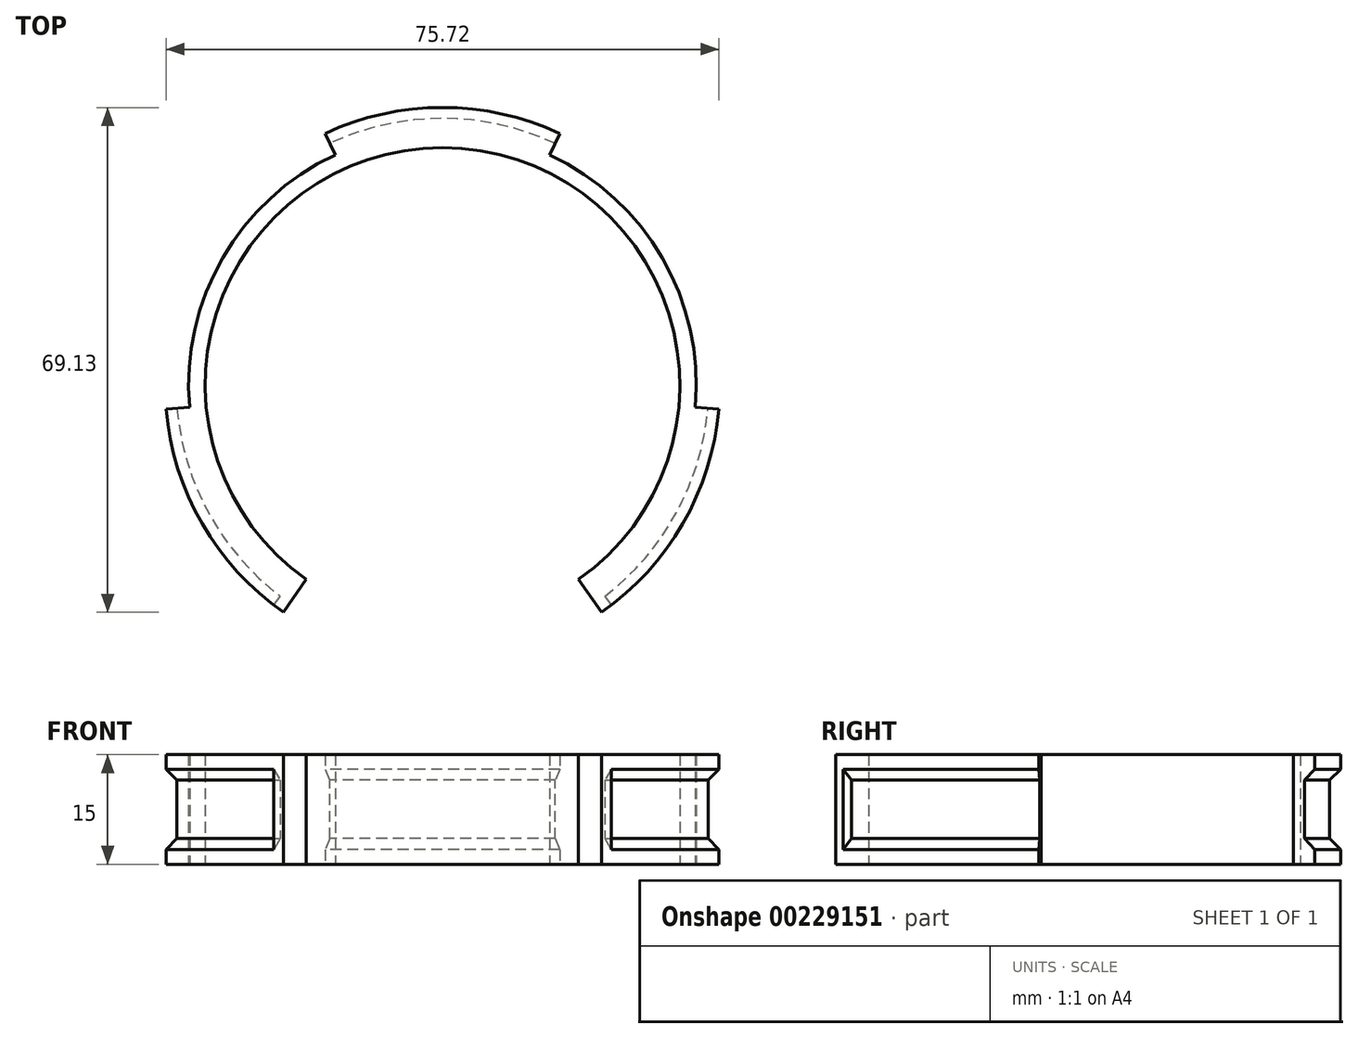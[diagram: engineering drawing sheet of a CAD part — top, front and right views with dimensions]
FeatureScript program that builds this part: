
annotation { "Feature Type Name" : "Feature", "Feature Type Description" : "" }
export const myFeature = defineFeature(function(context is Context, id is Id, definition is map)
    precondition{}
    {
        {
            var Q0;
            Q0=qCreatedBy(makeId("Top.planeOp"),FACE);
            var sketch = newSketch(context, id + "F0", { "sketchPlane" : qUnion([Q0])});
            skArc(sketch, "E0", {"start": v(21.8, -31.13) * mm, "mid": v(32.9, -19) * mm, "end": v(37.86, -3.31) * mm});
            skArc(sketch, "E1", {"start": v(18.64, -26.62) * mm, "mid": v(0, 32.5) * mm, "end": v(-18.64, -26.62) * mm});
            skLineSegment(sketch, "E2", {"start": v(18.64, -26.62) * mm, "end": v(21.8, -31.13) * mm});
            skLineSegment(sketch, "E3", {"start": v(0, -60.58) * mm, "end": v(0, 54.66) * mm, "construction": true});
            skLineSegment(sketch, "E4.MirrorCS", {"start": v(-18.64, -26.62) * mm, "end": v(-21.8, -31.13) * mm});
            skLineSegment(sketch, "E5", {"start": v(0, 0) * mm, "end": v(-69.84, -40.32) * mm, "construction": true});
            skArc(sketch, "E6.trimOffspring", {"start": v(-37.86, -3.31) * mm, "mid": v(-32.9, -19) * mm, "end": v(-21.8, -31.13) * mm});
            skArc(sketch, "E7.trimOffspring", {"start": v(16.06, 34.44) * mm, "mid": v(0, 38) * mm, "end": v(-16.06, 34.44) * mm});
            skPoint(sketch, "E8.orphan", {"position": v(-13.74, 29.46) * mm});
            skPoint(sketch, "E9.orphan", {"position": v(13.74, 29.46) * mm});
            skPoint(sketch, "E10.orphan", {"position": v(-32.38, -2.83) * mm});
            skPoint(sketch, "E11.orphan", {"position": v(32.38, -2.83) * mm});
            skPoint(sketch, "E12.visualSharp", {"position": v(-18.73, 40.16) * mm});
            skPoint(sketch, "E13.visualSharp", {"position": v(18.73, 40.16) * mm});
            skPoint(sketch, "E14.visualSharp", {"position": v(44.14, -3.86) * mm});
            skPoint(sketch, "E15.visualSharp", {"position": v(-44.14, -3.86) * mm});
            skArc(sketch, "E16", {"start": v(34.63, -3.03) * mm, "mid": v(30.1, 17.38) * mm, "end": v(14.7, 31.5) * mm});
            skLineSegment(sketch, "E17", {"start": v(-34.63, -3.03) * mm, "end": v(-37.86, -3.31) * mm});
            skLineSegment(sketch, "E18", {"start": v(34.63, -3.03) * mm, "end": v(37.86, -3.31) * mm});
            skLineSegment(sketch, "E19.trimOffspring", {"start": v(14.7, 31.5) * mm, "end": v(16.06, 34.44) * mm});
            skPoint(sketch, "E20.orphan", {"position": v(12.61, 0) * mm});
            skArc(sketch, "E21.trimOffspring", {"start": v(-14.7, 31.5) * mm, "mid": v(-30.1, 17.38) * mm, "end": v(-34.63, -3.03) * mm});
            skLineSegment(sketch, "E22", {"start": v(-14.7, 31.5) * mm, "end": v(-16.06, 34.44) * mm});
            skPoint(sketch, "E23.orphan", {"position": v(-13.74, 31.93) * mm});
            skSolve(sketch);
        }
        {
            var Q0;
            Q0=qSketchRegion(id+"F0",true);
            extrude(context, id + "F1", {"entities" : qUnion([Q0]), "depth" : 15 * mm, "offsetDistance" : 25 * mm});
        }
        {
            var Q0;
            Q0=qCreatedBy(makeId("Front.planeOp"),FACE);
            var sketch = newSketch(context, id + "F2", { "sketchPlane" : qUnion([Q0])});
            skLineSegment(sketch, "E24", {"start": v(0, -36.51) * mm, "end": v(0, 59.07) * mm, "construction": true});
            skSolve(sketch);
        }
        {
            var Q0;
            Q0=qCreatedBy(makeId("Right.planeOp"),FACE);
            var sketch = newSketch(context, id + "F3", { "sketchPlane" : qUnion([Q0])});
            skLineSegment(sketch, "E25", {"start": v(36.5, 11.5) * mm, "end": v(36.5, 3.5) * mm});
            skLineSegment(sketch, "E26", {"start": v(36.5, 3.5) * mm, "end": v(38, 2) * mm});
            skLineSegment(sketch, "E27", {"start": v(38, 2) * mm, "end": v(38, 0) * mm});
            skLineSegment(sketch, "E28", {"start": v(40.65, 0) * mm, "end": v(38, 0) * mm});
            skLineSegment(sketch, "E29", {"start": v(40.65, 0) * mm, "end": v(40.65, 15) * mm});
            skLineSegment(sketch, "E30", {"start": v(38, 15) * mm, "end": v(40.65, 15) * mm});
            skLineSegment(sketch, "E31", {"start": v(38, 15) * mm, "end": v(38, 13) * mm});
            skLineSegment(sketch, "E32", {"start": v(38, 13) * mm, "end": v(36.5, 11.5) * mm});
            skLineSegment(sketch, "E33", {"start": v(38, -4.58) * mm, "end": v(38, 19.18) * mm, "construction": true});
            skSolve(sketch);
        }
        {
            var Q0;
            Q0 = qSketchRegion(id + "F3", true);
            var Q1;
            Q1=sQuery(id+"F2.wireOp",EDGE,"E24");
            revolve(context, id + "F4", {"operationType" : NewBodyOperationType.REMOVE, "surfaceOperationType" : NewSurfaceOperationType.NEW, "entities" : qUnion([Q0]), "axis" : qUnion([Q1]), "revolveType" : RevolveType.SYMMETRIC, "oppositeDirection" : true, "angle" : 285 * degree});
        }
    });
